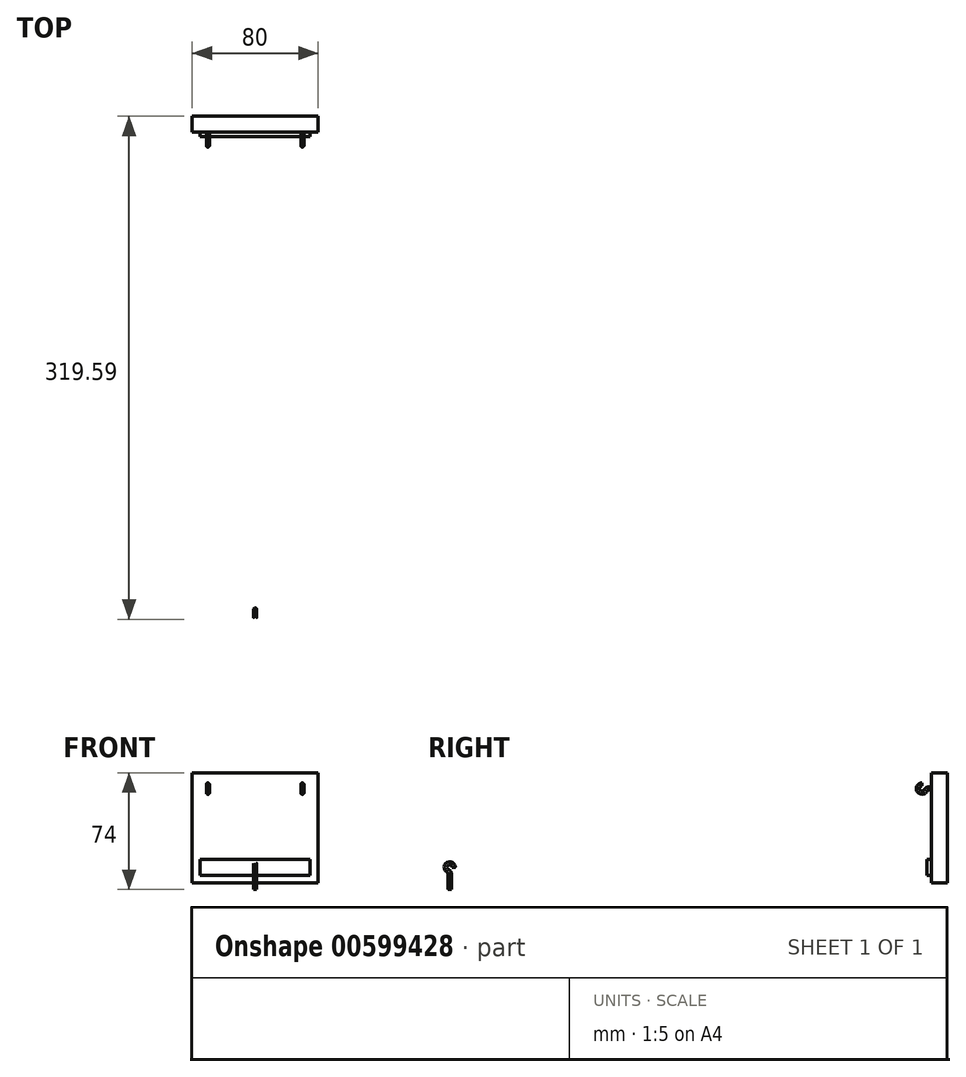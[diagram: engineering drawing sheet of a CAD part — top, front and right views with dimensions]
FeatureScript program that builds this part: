
annotation { "Feature Type Name" : "Feature", "Feature Type Description" : "" }
export const myFeature = defineFeature(function(context is Context, id is Id, definition is map)
    precondition{}
    {
        {
            var Q0;
            Q0=qCreatedBy(makeId("Front.planeOp"),FACE);
            var sketch = newSketch(context, id + "F0", { "sketchPlane" : qUnion([Q0])});
            skLineSegment(sketch, "E0.bottom", {"start": v(30, 0) * mm, "end": v(-30, 0) * mm, "construction": true});
            skLineSegment(sketch, "E0.top", {"start": v(30, 50) * mm, "end": v(-30, 50) * mm, "construction": true});
            skLineSegment(sketch, "E0.left", {"start": v(30, 0) * mm, "end": v(30, 50) * mm, "construction": true});
            skLineSegment(sketch, "E0.right", {"start": v(-30, 0) * mm, "end": v(-30, 50) * mm, "construction": true});
            skPoint(sketch, "E0.middle", {"position": v(0, 25) * mm});
            skLineSegment(sketch, "E1.0", {"start": v(40, 60) * mm, "end": v(-40, 60) * mm});
            skLineSegment(sketch, "E1.1", {"start": v(40, -10) * mm, "end": v(40, 60) * mm});
            skLineSegment(sketch, "E1.2", {"start": v(40, -10) * mm, "end": v(-40, -10) * mm});
            skLineSegment(sketch, "E1.3", {"start": v(-40, -10) * mm, "end": v(-40, 60) * mm});
            skSolve(sketch);
        }
        {
            var Q0;
            Q0=qSketchRegion(id+"F0",true);
            var Q1;
            Q1=qConstructionFilter(qBodyType(qCreatedBy(id+"F0",EDGE),BodyType.WIRE),ConstructionObject.NO);
            extrude(context, id + "F1", {"entities" : qUnion([Q0]), "surfaceEntities" : qUnion([Q1]), "oppositeDirection" : true, "depth" : 10 * mm, "offsetDistance" : 25 * mm});
        }
        {
            var Q0;
            Q0=qCreatedBy(makeId("Right.planeOp"),FACE);
            cPlane(context, id + "F2", {"entities" : qUnion([Q0]), "cplaneType" : CPlaneType.OFFSET, "offset" : 30 * mm, "width" : 150 * mm, "height" : 150 * mm});
        }
        {
            var Q0;
            Q0=qCreatedBy(makeId("Right.planeOp"),FACE);
            cPlane(context, id + "F3", {"entities" : qUnion([Q0]), "cplaneType" : CPlaneType.OFFSET, "offset" : 30 * mm, "oppositeDirection" : true, "width" : 150 * mm, "height" : 150 * mm});
        }
        {
            var Q0;
            Q0=qCreatedBy(id+"F3.planeOp",FACE);
            var sketch = newSketch(context, id + "F4", { "sketchPlane" : qUnion([Q0])});
            skLineSegment(sketch, "E2", {"start": v(0, 50) * mm, "end": v(-2, 50) * mm});
            skArc(sketch, "E3", {"start": v(-2, 50) * mm, "mid": v(-2.98, 49.71) * mm, "end": v(-3.64, 48.94) * mm});
            skArc(sketch, "E4", {"start": v(-3.64, 48.94) * mm, "mid": v(-8.17, 48.6) * mm, "end": v(-6, 52.59) * mm});
            skLineSegment(sketch, "E5", {"start": v(0, 50) * mm, "end": v(-6, 50) * mm, "construction": true});
            skSolve(sketch);
        }
        {
            var Q0;
            Q0=makeQuery(id+"F1.opExtrude","CAP_FACE",FACE,{"disambiguationData":[OSD([sQuery(id+"F0.wireOp",EDGE,"E1.0"),sQuery(id+"F0.wireOp",EDGE,"E1.1"),sQuery(id+"F0.wireOp",EDGE,"E1.2"),sQuery(id+"F0.wireOp",EDGE,"E1.3")])],"isStart":true});
            var sketch = newSketch(context, id + "F5", { "sketchPlane" : qUnion([Q0])});
            skCircle(sketch, "E6", {"center": v(-30, 50) * mm, "radius": 1 * mm});
            skSolve(sketch);
        }
        {
            var Q0;
            Q0=makeQuery(id+"F5.imprint","IMPRINT",FACE,{"disambiguationData":[TD([[makeQuery(id+"F5.imprint","IMPRINT",EDGE,{"derivedFrom":sQuery(id+"F5.wireOp",EDGE,"E6")}),1.0]])]});
            var Q1;
            Q1=qConstructionFilter(qBodyType(qCreatedBy(id+"F4",EDGE),BodyType.WIRE),ConstructionObject.NO);
            sweep(context, id + "F6", {"profiles" : qUnion([Q0]), "path" : qUnion([Q1])});
        }
        {
            var Q0;
            Q0=makeQuery(id+"F6.opSweep","SWEPT_BODY",BODY,{"disambiguationData":[OSD([sQuery(id+"F4.wireOp",EDGE,"E4"),sQuery(id+"F5.wireOp",EDGE,"E6")])]});
            var Q1;
            Q1=qCreatedBy(makeId("Right.planeOp"),FACE);
            mirror(context, id + "F7", {"operationType" : NewBodyOperationType.ADD, "entities" : qUnion([Q0]), "mirrorPlane" : qUnion([Q1])});
        }
        {
            var Q0;
            Q0=makeQuery(id+"F1.opExtrude","CAP_FACE",FACE,{"disambiguationData":[OSD([sQuery(id+"F0.wireOp",EDGE,"E1.0"),sQuery(id+"F0.wireOp",EDGE,"E1.1"),sQuery(id+"F0.wireOp",EDGE,"E1.2"),sQuery(id+"F0.wireOp",EDGE,"E1.3")])],"isStart":true});
            var sketch = newSketch(context, id + "F8", { "sketchPlane" : qUnion([Q0])});
            skLineSegment(sketch, "E7.bottom", {"start": v(35, -5) * mm, "end": v(-35, -5) * mm});
            skLineSegment(sketch, "E7.top", {"start": v(35, 5) * mm, "end": v(-35, 5) * mm});
            skLineSegment(sketch, "E7.left", {"start": v(35, -5) * mm, "end": v(35, 5) * mm});
            skLineSegment(sketch, "E7.right", {"start": v(-35, -5) * mm, "end": v(-35, 5) * mm});
            skPoint(sketch, "E7.middle", {"position": v(0, 0) * mm});
            skSolve(sketch);
        }
        {
            var Q0;
            Q0=qSketchRegion(id+"F8",true);
            extrude(context, id + "F9", {"entities" : qUnion([Q0]), "operationType" : NewBodyOperationType.ADD, "depth" : 3 * mm, "offsetDistance" : 25 * mm});
        }
        {
            var Q0;
            Q0=makeQuery(id+"F1.opExtrude","SWEPT_BODY",BODY,{"disambiguationData":[OSD([sQuery(id+"F0.wireOp",EDGE,"E1.0"),sQuery(id+"F0.wireOp",EDGE,"E1.1"),sQuery(id+"F0.wireOp",EDGE,"E1.2"),sQuery(id+"F0.wireOp",EDGE,"E1.3")])]});
            var Q1;
            Q1=sQuery(id+"F4.wireOp",EDGE,"E5");
            transform(context, id + "F10", {"entities" : qUnion([Q0]), "transformType" : TransformType.TRANSLATION_ENTITY, "oppositeDirectionEntity" : true, "transformLine" : qUnion([Q1]), "makeCopy" : false});
        }
        {
            var Q0;
            Q0=qCreatedBy(makeId("Right.planeOp"),FACE);
            var sketch = newSketch(context, id + "F11", { "sketchPlane" : qUnion([Q0])});
            skLineSegment(sketch, "E8", {"start": v(-300, -14) * mm, "end": v(-300, -4) * mm});
            skArc(sketch, "E9", {"start": v(-300, -4) * mm, "mid": v(-300.29, -3.02) * mm, "end": v(-301.06, -2.36) * mm});
            skArc(sketch, "E10", {"start": v(-301.06, -2.36) * mm, "mid": v(-301.4, 2.17) * mm, "end": v(-297.41, 0) * mm});
            skSolve(sketch);
        }
        {
            var Q0;
            Q0=qCreatedBy(makeId("Top.planeOp"),FACE);
            var sketch = newSketch(context, id + "F12", { "sketchPlane" : qUnion([Q0])});
            skCircle(sketch, "E11", {"center": v(0, -297.41) * mm, "radius": 1 * mm});
            skSolve(sketch);
        }
        {
            var Q0;
            Q0=qSketchRegion(id+"F12",true);
            var Q1;
            Q1=qConstructionFilter(qBodyType(qCreatedBy(id+"F11",EDGE),BodyType.WIRE),ConstructionObject.NO);
            sweep(context, id + "F13", {"profiles" : qUnion([Q0]), "path" : qUnion([Q1])});
        }
    });
